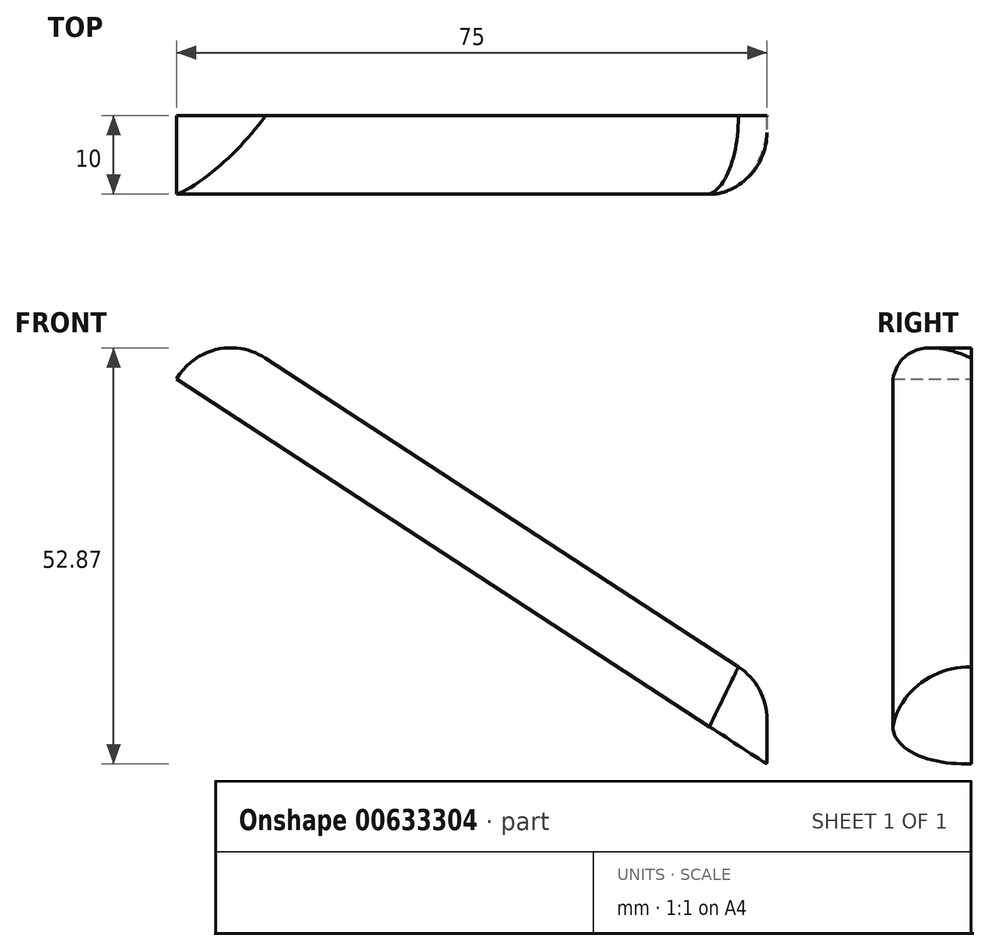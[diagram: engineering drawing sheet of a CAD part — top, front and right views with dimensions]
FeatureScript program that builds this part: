
annotation { "Feature Type Name" : "Feature", "Feature Type Description" : "" }
export const myFeature = defineFeature(function(context is Context, id is Id, definition is map)
    precondition{}
    {
        {
            var Q0;
            Q0=qCreatedBy(makeId("Front.planeOp"),FACE);
            var sketch = newSketch(context, id + "F0", { "sketchPlane" : qUnion([Q0])});
            skLineSegment(sketch, "E0", {"start": v(-37.5, 58.78) * mm, "end": v(-37.5, -69.07) * mm, "construction": true});
            skLineSegment(sketch, "E1", {"start": v(37.5, 60.72) * mm, "end": v(37.5, -69.85) * mm, "construction": true});
            skLineSegment(sketch, "E2", {"start": v(-37.5, 21.12) * mm, "end": v(37.5, -27.83) * mm});
            skLineSegment(sketch, "E3", {"start": v(37.5, -27.83) * mm, "end": v(37.5, -37.83) * mm});
            skLineSegment(sketch, "E4", {"start": v(37.5, -37.83) * mm, "end": v(-37.5, 11.12) * mm});
            skLineSegment(sketch, "E5", {"start": v(-37.5, 11.12) * mm, "end": v(-37.5, 21.12) * mm});
            skSolve(sketch);
        }
        {
            var Q0;
            Q0 = qSketchRegion(id + "F0", true);
            extrude(context, id + "F1", {"entities" : qUnion([Q0]), "depth" : 10 * mm, "offsetDistance" : 25 * mm});
        }
        {
            var Q0;
            Q0=makeQuery(id+"F1.opExtrude","CAP_EDGE",EDGE,{"disambiguationData":[OSD([sQuery(id+"F0.wireOp",EDGE,"E2")])],"isStart":false});
            fillet(context, id + "F2", {"entities" : qUnion([Q0]), "radius" : 10 * mm, "tangentPropagation" : true, "allowEdgeOverflow" : false});
        }
        {
            var Q0;
            Q0=makeQuery(id+"F2.opFillet","BLEND_EDGE",EDGE,{"blendedFrom":[makeQuery(id+"F1.opExtrude","CAP_EDGE",EDGE,{"disambiguationData":[OSD([sQuery(id+"F0.wireOp",EDGE,"E2")])],"isStart":false}),makeQuery(id+"F1.opExtrude","SWEPT_FACE",FACE,{"disambiguationData":[OSD([sQuery(id+"F0.wireOp",EDGE,"E3")])]})],"blendedInto":[makeQuery(id+"F1.opExtrude","SWEPT_FACE",FACE,{"disambiguationData":[OSD([sQuery(id+"F0.wireOp",EDGE,"E3")])]})]});
            var Q1;
            Q1=makeQuery(id+"F2.opFillet","BLEND_EDGE",EDGE,{"blendedFrom":[makeQuery(id+"F1.opExtrude","CAP_EDGE",EDGE,{"disambiguationData":[OSD([sQuery(id+"F0.wireOp",EDGE,"E2")])],"isStart":false}),makeQuery(id+"F1.opExtrude","SWEPT_FACE",FACE,{"disambiguationData":[OSD([sQuery(id+"F0.wireOp",EDGE,"E5")])]})],"blendedInto":[makeQuery(id+"F1.opExtrude","SWEPT_FACE",FACE,{"disambiguationData":[OSD([sQuery(id+"F0.wireOp",EDGE,"E5")])]})]});
            fillet(context, id + "F3", {"entities" : qUnion([Q0, Q1]), "radius" : 8 * mm, "tangentPropagation" : true, "allowEdgeOverflow" : false});
        }
    });
